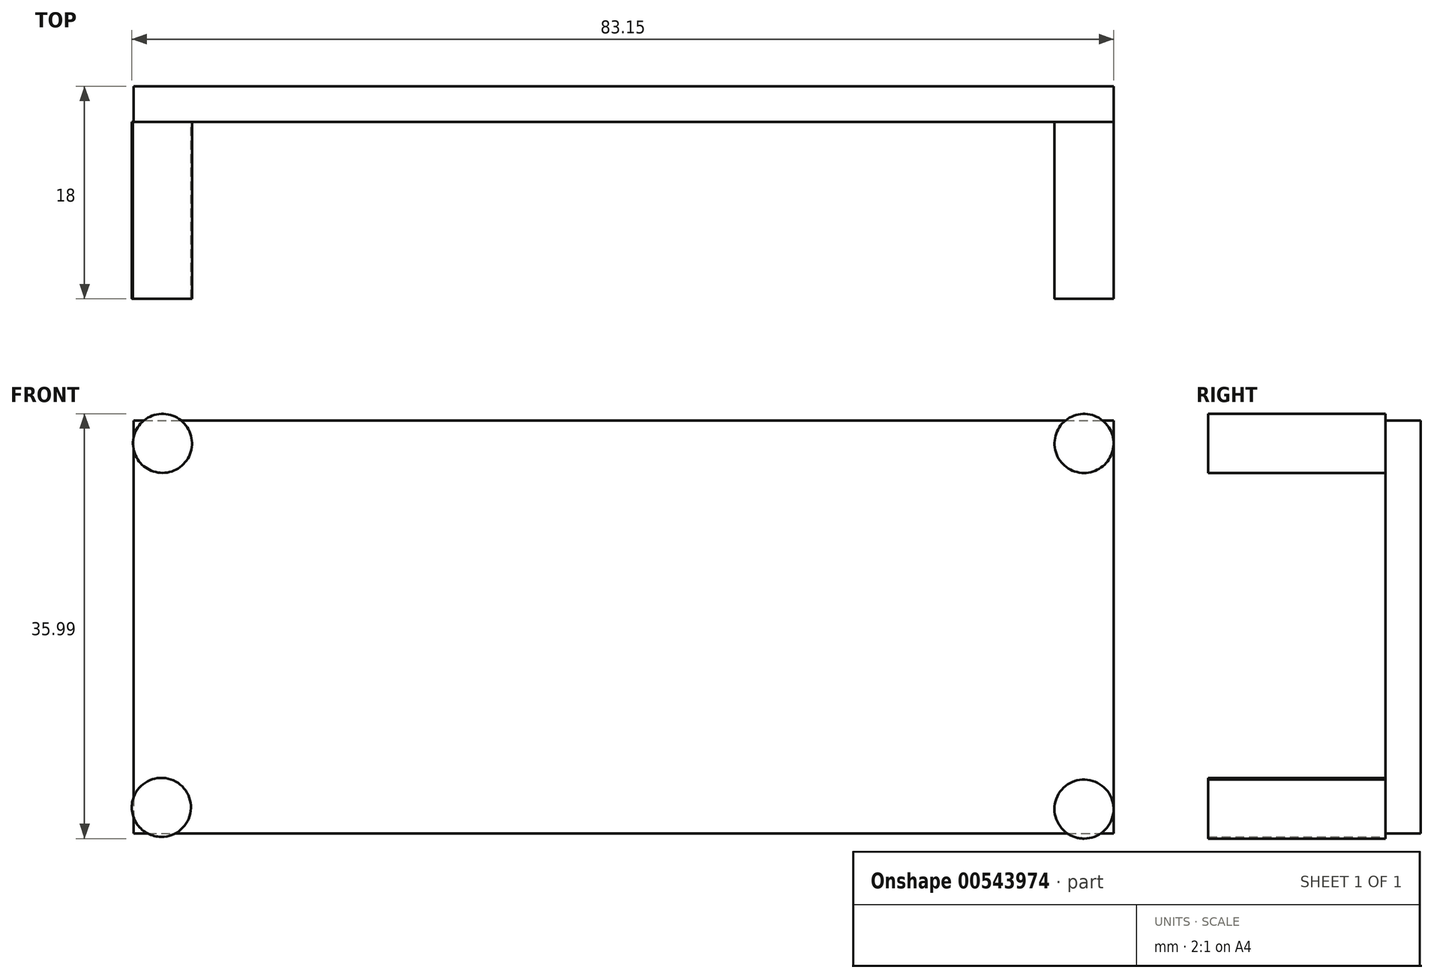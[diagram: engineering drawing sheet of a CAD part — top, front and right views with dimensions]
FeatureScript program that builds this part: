
annotation { "Feature Type Name" : "Feature", "Feature Type Description" : "" }
export const myFeature = defineFeature(function(context is Context, id is Id, definition is map)
    precondition{}
    {
        {
            var Q0;
            Q0=qCreatedBy(makeId("Front.planeOp"),FACE);
            var sketch = newSketch(context, id + "F0", { "sketchPlane" : qUnion([Q0])});
            skLineSegment(sketch, "E0.bottom", {"start": v(-41.5, 17.5) * mm, "end": v(41.5, 17.5) * mm});
            skLineSegment(sketch, "E0.top", {"start": v(-41.5, -17.5) * mm, "end": v(41.5, -17.5) * mm});
            skLineSegment(sketch, "E0.left", {"start": v(-41.5, 17.5) * mm, "end": v(-41.5, -17.5) * mm});
            skLineSegment(sketch, "E0.right", {"start": v(41.5, 17.5) * mm, "end": v(41.5, -17.5) * mm});
            skPoint(sketch, "E0.middle", {"position": v(0, 0) * mm});
            skSolve(sketch);
        }
        {
            var Q0;
            Q0=makeQuery(id+"F0.imprint","IMPRINT",FACE,{"disambiguationData":[TD([[makeQuery(id+"F0.imprint","IMPRINT",EDGE,{"derivedFrom":sQuery(id+"F0.wireOp",EDGE,"E0.bottom")}),-1.0]])]});
            extrude(context, id + "F1", {"entities" : qUnion([Q0]), "depth" : 3 * mm, "offsetDistance" : 25 * mm});
        }
        {
            var Q0;
            Q0=makeQuery(id+"F1.opExtrude","CAP_FACE",FACE,{"disambiguationData":[OSD([sQuery(id+"F0.wireOp",EDGE,"E0.bottom"),sQuery(id+"F0.wireOp",EDGE,"E0.top"),sQuery(id+"F0.wireOp",EDGE,"E0.left"),sQuery(id+"F0.wireOp",EDGE,"E0.right")])],"isStart":false});
            var sketch = newSketch(context, id + "F2", { "sketchPlane" : qUnion([Q0])});
            skLineSegment(sketch, "E1.bottom", {"start": v(41.5, 17.5) * mm, "end": v(36.5, 17.5) * mm});
            skLineSegment(sketch, "E1.top", {"start": v(41.5, 13.43) * mm, "end": v(36.5, 13.43) * mm});
            skLineSegment(sketch, "E1.left", {"start": v(41.5, 17.5) * mm, "end": v(41.5, 13.43) * mm});
            skLineSegment(sketch, "E1.right", {"start": v(36.5, 17.5) * mm, "end": v(36.5, 13.43) * mm});
            skLineSegment(sketch, "E2.bottom", {"start": v(41.5, -17.5) * mm, "end": v(36.5, -17.5) * mm});
            skLineSegment(sketch, "E2.top", {"start": v(41.5, -13.42) * mm, "end": v(36.5, -13.42) * mm});
            skLineSegment(sketch, "E2.left", {"start": v(41.5, -17.5) * mm, "end": v(41.5, -13.42) * mm});
            skLineSegment(sketch, "E2.right", {"start": v(36.5, -17.5) * mm, "end": v(36.5, -13.42) * mm});
            skLineSegment(sketch, "E3.bottom", {"start": v(-41.5, -17.5) * mm, "end": v(-36.16, -17.5) * mm});
            skLineSegment(sketch, "E3.top", {"start": v(-41.5, -12.93) * mm, "end": v(-36.16, -12.93) * mm});
            skLineSegment(sketch, "E3.left", {"start": v(-41.5, -17.5) * mm, "end": v(-41.5, -12.93) * mm});
            skLineSegment(sketch, "E3.right", {"start": v(-36.16, -17.5) * mm, "end": v(-36.16, -12.93) * mm});
            skLineSegment(sketch, "E4.bottom", {"start": v(-41.5, 17.5) * mm, "end": v(-36.5, 17.5) * mm});
            skLineSegment(sketch, "E4.top", {"start": v(-41.5, 13.43) * mm, "end": v(-36.5, 13.43) * mm});
            skLineSegment(sketch, "E4.left", {"start": v(-41.5, 17.5) * mm, "end": v(-41.5, 13.43) * mm});
            skLineSegment(sketch, "E4.right", {"start": v(-36.5, 17.5) * mm, "end": v(-36.5, 13.43) * mm});
            skSolve(sketch);
        }
        {
            var Q0;
            Q0=makeQuery(id+"F2.imprint","IMPRINT",FACE,{"disambiguationData":[TD([[makeQuery(id+"F2.imprint","IMPRINT",EDGE,{"derivedFrom":sQuery(id+"F2.wireOp",EDGE,"E4.bottom")}),-1.0]])]});
            var sketch = newSketch(context, id + "F3", { "sketchPlane" : qUnion([Q0])});
            skCircle(sketch, "E5", {"center": v(-39.06, 15.56) * mm, "radius": 2.5 * mm});
            skSolve(sketch);
        }
        {
            var Q0;
            Q0=makeQuery(id+"F2.imprint","IMPRINT",FACE,{"disambiguationData":[TD([[makeQuery(id+"F2.imprint","IMPRINT",EDGE,{"derivedFrom":sQuery(id+"F2.wireOp",EDGE,"E1.bottom")}),-1.0]])]});
            var sketch = newSketch(context, id + "F4", { "sketchPlane" : qUnion([Q0])});
            skCircle(sketch, "E6", {"center": v(38.98, 15.55) * mm, "radius": 2.5 * mm});
            skSolve(sketch);
        }
        {
            var Q0;
            Q0=makeQuery(id+"F2.imprint","IMPRINT",FACE,{"disambiguationData":[TD([[makeQuery(id+"F2.imprint","IMPRINT",EDGE,{"derivedFrom":sQuery(id+"F2.wireOp",EDGE,"E2.bottom")}),1.0]])]});
            var sketch = newSketch(context, id + "F5", { "sketchPlane" : qUnion([Q0])});
            skCircle(sketch, "E7", {"center": v(38.98, -15.43) * mm, "radius": 2.5 * mm});
            skSolve(sketch);
        }
        {
            var Q0;
            Q0=makeQuery(id+"F2.imprint","IMPRINT",FACE,{"disambiguationData":[TD([[makeQuery(id+"F2.imprint","IMPRINT",EDGE,{"derivedFrom":sQuery(id+"F2.wireOp",EDGE,"E3.bottom")}),1.0]])]});
            var sketch = newSketch(context, id + "F6", { "sketchPlane" : qUnion([Q0])});
            skCircle(sketch, "E8", {"center": v(-39.15, -15.29) * mm, "radius": 2.5 * mm});
            skSolve(sketch);
        }
        {
            var Q0;
            Q0=qSketchRegion(id+"F6",true);
            extrude(context, id + "F7", {"entities" : qUnion([Q0]), "operationType" : NewBodyOperationType.ADD, "depth" : 15 * mm, "offsetDistance" : 25 * mm});
        }
        {
            var Q0;
            Q0=qSketchRegion(id+"F3",true);
            extrude(context, id + "F8", {"entities" : qUnion([Q0]), "operationType" : NewBodyOperationType.ADD, "depth" : 15 * mm, "offsetDistance" : 25 * mm});
        }
        {
            var Q0;
            Q0=qSketchRegion(id+"F4",true);
            extrude(context, id + "F9", {"entities" : qUnion([Q0]), "operationType" : NewBodyOperationType.ADD, "depth" : 15 * mm, "offsetDistance" : 25 * mm});
        }
        {
            var Q0;
            Q0=qSketchRegion(id+"F6",true);
            extrude(context, id + "F10", {"entities" : qUnion([Q0]), "operationType" : NewBodyOperationType.ADD, "depth" : 15 * mm, "offsetDistance" : 25 * mm});
        }
        {
            var Q0;
            Q0=qSketchRegion(id+"F5",true);
            extrude(context, id + "F11", {"entities" : qUnion([Q0]), "operationType" : NewBodyOperationType.ADD, "depth" : 15 * mm, "offsetDistance" : 25 * mm});
        }
    });
